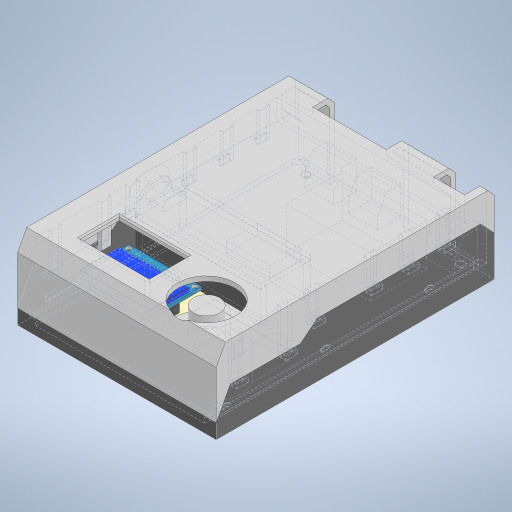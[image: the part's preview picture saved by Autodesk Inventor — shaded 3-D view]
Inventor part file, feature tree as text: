
AUTODESK INVENTOR PART (.ipt)
format: ipt  version: 2024.1 (Build 281209000, 209)  size: 1,683,456 bytes
history: native  units: mm
features: sketch x53, extrude x52, projected_geometry x36, chamfer x13, fillet x5, other x3, mirror x2, pattern_linear x1, plane x1
ambient origin geometry x8: Origin, YZ Plane, XZ Plane, XY Plane, X Axis, Y Axis, Z Axis, Center Point
bodies: Body1 (feature_tree), Body2 (feature_tree), Body3 (feature_tree)
feature tree (166):
  other  "pcb"
  extrude  "Extrusion1"  Depth=95.0mm
  chamfer  "Chamfer1"  Distance=1.57mm
  extrude  "Extrusion2"  Depth=10.8mm
  chamfer  "Chamfer2"  Distance=10.12mm
  chamfer  "Chamfer19"  Distance=3.0mm Angle=45.0deg
  chamfer  "Chamfer20"  Distance=15.0mm
  extrude  "Extrusion3"  Depth=1.2mm
  extrude  "Extrusion5"  Depth=17.9mm
  extrude  "Extrusion6"  Depth=2.44mm
  extrude  "Extrusion7"  Depth=0.1mm TaperAngle=0.0deg
  fillet  "Fillet1"  Radius=0.1mm
  fillet  "Fillet2"  Radius=5.0mm
  extrude  "Extrusion14"  Depth=5.0mm
  extrude  "Extrusion8"  Depth=3.2mm TaperAngle=0.0deg
  extrude  "Extrusion9"  Depth=2.0mm
  extrude  "Extrusion10"  Depth=2.37mm
  sketch  "Sketch12"  dims[d21=30.0mm d22=15.0mm d23=0.0mm]
  extrude  "Extrusion11"  Depth=10.2mm
  extrude  "Extrusion12"  Depth=0.1mm
  fillet  "Fillet3"  Radius=0.1mm
  extrude  "Extrusion13"  Depth=26.0mm
  extrude  "Extrusion88"  Depth=0.56mm
  extrude  "Extrusion89"  Depth=4.0mm
  fillet  "Fillet10"  Radius=16.58mm
  extrude  "Extrusion90"  Depth=0.1mm
  extrude  "Extrusion23"  Depth=0.1mm
  chamfer  "Chamfer3"  Distance=0.2mm
  pattern_linear  "Rectangular Pattern1"  Count1=2 Spacing1=55.0mm
  extrude  "CASE - START"  Depth=2.0mm
  extrude  "Extrusion25"  Depth=2.0mm
  extrude  "Extrusion26"  Depth=0.2mm
  chamfer  "Chamfer4"  Distance=1.64mm
  extrude  "Extrusion27"  Depth=0.5mm
  extrude  "Extrusion28"  Depth=13.0mm
  extrude  "Extrusion29"  Depth=0.5mm
  chamfer  "Chamfer5"  Distance=1.64mm
  fillet  "Fillet7"  Radius=4.0mm
  extrude  "Extrusion30"  Depth=1.5mm
  chamfer  "Chamfer6"  Distance=3.3mm
  extrude  "Extrusion33"  Depth=0.5mm TaperAngle=0.0deg
  extrude  "Extrusion35"  Depth=0.5mm
  chamfer  "Chamfer7"  Distance=0.5mm
  extrude  "Extrusion39"  Depth=0.5mm TaperAngle=0.0deg
  extrude  "Extrusion75"  Depth=0.5mm
  chamfer  "Chamfer9"  Distance=5.0mm
  extrude  "Extrusion79"  Depth=0.5mm
  extrude  "Extrusion80"  Depth=0.8mm
  extrude  "Extrusion81"  Depth=2.0mm TaperAngle=0.0deg
  extrude  "Extrusion91"  Depth=2.0mm TaperAngle=45.0deg
  extrude  "Extrusion83"  Depth=0.5mm
  extrude  "Extrusion53"  TaperAngle=0.0deg  [1 undecoded]
  extrude  "Extrusion92"  Depth=0.5mm
  extrude  "base-slots"  Depth=10.0mm
  extrude  "Extrusion62"  Depth=0.5mm
  extrude  "Extrusion63"  [1 undecoded]
  extrude  "Extrusion64"  Depth=0.5mm
  extrude  "Extrusion65"  Depth=0.5mm
  extrude  "Extrusion66"  Depth=0.5mm
  sketch  "Sketch78"  dims[d81=23.5mm]
  extrude  "Extrusion93"  Depth=0.5mm
  extrude  "Extrusion94"  Depth=2.0mm TaperAngle=0.0deg
  extrude  "Extrusion68"  Depth=2.0mm TaperAngle=45.0deg
  extrude  "Extrusion69"  Depth=1.5mm TaperAngle=0.0deg
  extrude  "Extrusion70"  Depth=0.5mm TaperAngle=0.0deg
  extrude  "Extrusion71"  Depth=2.0mm TaperAngle=45.0deg
  extrude  "Extrusion95"  Depth=0.5mm TaperAngle=0.0deg
  extrude  "Extrusion96"  Depth=0.5mm TaperAngle=45.0deg
  plane  "Work Plane1"
  chamfer  "Chamfer13"  Distance=10.0mm
  mirror  "Mirror1"
  mirror  "Mirror2"
  extrude  "Extrusion85"  Depth=1.5mm
  extrude  "Extrusion86"  Depth=2.0mm
  chamfer  "Chamfer15"  Distance=4.0mm
  chamfer  "Chamfer16"  Distance=4.0mm
  extrude  "Extrusion87"  Depth=2.0mm
  sketch  "Sketch1"  dims[d0=64.4mm d1=95.0mm]
  sketch  "Sketch2"  dims[d2=47.5mm]
  sketch  "Sketch3"  dims[d3=32.2mm d4=1.57mm d5=0.0mm]
  sketch  "Sketch5"  dims[d6=2.0mm d7=2.0mm d8=45.0deg d9=10.8mm]
  sketch  "Sketch7"  dims[d10=8.8mm]
  sketch  "Sketch8"  dims[d12=8.2mm d13=10.12mm d14=0.0mm d15=3.0mm d16=6.0mm d17=45.0deg]
  sketch  "Sketch9"  dims[d18=12.0mm]
  sketch  "Sketch10"  dims[d19=20.0mm]
  sketch  "Sketch11"  dims[d20=6.26mm]
  sketch  "Sketch13"  dims[d30=41.24mm d31=1.2mm]
  sketch  "Sketch14"  dims[d32=44.25mm d33=17.9mm]
  sketch  "Sketch15"  dims[d34=2.44mm d36=2.44mm]
  sketch  "Sketch17"  dims[d37=11.2mm d38=0.0mm d39=1.63mm d40=0.0mm d41=0.1mm d42=5.0mm]
  sketch  "Sketch26"  dims[d43=1.3mm d44=5.0mm]
  sketch  "Sketch28"  dims[d45=5.0mm d46=3.2mm d47=0.0mm]
  other  "case-bottom"
  sketch  "Sketch29"  dims[d48=2.0mm d49=3.0mm]
  projected_geometry  "Projected Loop2"
  sketch  "Sketch30"  dims[d50=10.29mm d51=2.37mm]
  sketch  "Sketch32"  dims[d52=17.0mm d53=10.2mm]
  sketch  "Sketch33"  dims[d54=10.9mm d55=0.0mm d56=9.0mm d57=0.1mm]
  sketch  "Sketch34"  dims[d58=26.0mm d59=25.94mm]
  projected_geometry  "Projected Loop3"
  sketch  "Sketch35"  dims[d60=1.06mm d61=0.0mm d62=0.56mm]
  projected_geometry  "Projected Loop4"
  projected_geometry  "Projected Loop5"
  sketch  "Sketch38"  dims[d63=0.56mm d64=4.0mm d65=16.58mm]
  sketch  "Sketch39"  dims[d66=1.3mm d67=0.0mm d68=0.1mm]
  projected_geometry  "Projected Loop9"
  projected_geometry  "Projected Loop11"
  other  "lid-1"
  sketch  "Sketch46"  dims[d69=0.1mm d70=0.1mm]
  projected_geometry  "Projected Loop14"
  projected_geometry  "Projected Loop15"
  projected_geometry  "Projected Loop16"
  projected_geometry  "Projected Loop17"
  projected_geometry  "Projected Loop18"
  projected_geometry  "Projected Loop19"
  sketch  "Sketch61"  dims[d71=14.0mm d72=0.2mm d73=0.0mm]
  sketch  "Sketch70"  dims[d74=7.0mm]
  sketch  "Sketch71"  dims[d75=7.0mm]
  sketch  "Sketch72"  dims[d76=0.2mm]
  sketch  "Sketch73"  dims[d77=0.2mm]
  sketch  "Sketch74"  dims[d78=0.2mm d79=0.0mm]
  sketch  "Sketch75"  dims[d80=2.0mm]
  projected_geometry  "Projected Loop52"
  sketch  "Sketch79"  dims[d82=23.5mm]
  projected_geometry  "Projected Loop54"
  sketch  "Sketch80"  dims[d83=1.9mm]
  sketch  "Sketch81"  dims[d84=1.22mm]
  sketch  "Sketch85"  dims[d85=1.22mm]
  sketch  "Sketch89"  dims[d86=1.25mm]
  sketch  "Sketch90"  dims[d87=1.25mm]
  projected_geometry  "Projected Loop68"
  projected_geometry  "Projected Loop69"
  sketch  "Sketch91"  dims[d88=0.0mm d89=0.0mm]
  sketch  "Sketch93"  dims[d90=3.6mm]
  projected_geometry  "Projected Loop75"
  sketch  "Sketch95"  dims[d91=3.6mm]
  projected_geometry  "Projected Loop76"
  sketch  "Sketch96"  dims[d92=15.5mm]
  projected_geometry  "Projected Loop77"
  projected_geometry  "Projected Loop78"
  projected_geometry  "Projected Loop79"
  projected_geometry  "Projected Loop80"
  sketch  "Sketch97"  dims[d93=0.1mm]
  projected_geometry  "Projected Loop81"
  sketch  "Sketch98"  dims[d94=3.8mm d95=0.0mm]
  sketch  "Sketch100"  dims[d139=5.31mm]
  sketch  "Sketch101"  dims[d140=5.31mm]
  projected_geometry  "Projected Loop82"
  projected_geometry  "Projected Loop83"
  projected_geometry  "Projected Loop84"
  projected_geometry  "Projected Loop85"
  sketch  "Sketch102"  dims[d141=1.37mm d142=0.0mm]
  projected_geometry  "Projected Loop86"
  projected_geometry  "Projected Loop87"
  projected_geometry  "Projected Loop88"
  projected_geometry  "Projected Loop89"
  sketch  "Sketch103"  dims[d143=1.0mm d144=4.0mm d145=45.0deg d146=20.0mm d148=55.0mm d149=20.0mm d151=87.0mm]
  projected_geometry  "Projected Loop90"
  sketch  "Sketch104"  dims[d152=2.0mm d153=2.0mm]
  projected_geometry  "Projected Loop91"
  sketch  "Sketch105"  dims[d154=2.0mm d155=3.0mm]
  projected_geometry  "Projected Loop92"
  sketch  "Sketch106"  dims[d156=2.0mm d157=0.0mm d158=0.2mm d159=1.64mm d160=0.0mm]
  projected_geometry  "Projected Loop93"
  sketch  "Sketch107"  dims[d161=5.0mm d162=20.0mm d163=13.0mm d164=8.0mm d165=1.64mm d166=0.0mm d167=1.0mm d168=4.0mm d169=45.0deg d171=1.5mm d172=3.3mm d173=1.64mm d174=0.0mm d175=2.2mm d176=0.5mm d177=1.64mm d178=0.0mm d180=5.0mm d181=5.0mm d182=5.0mm d183=0.8mm d184=2.0mm d185=0.0mm d186=2.0mm d187=4.0mm d188=45.0deg d189=0.5mm d191=0.0mm d192=9.0mm d194=10.0mm d195=9.445mm d196=-2.445mm d197=5.0mm d198=30.0mm d199=1.2mm d200=1.7mm d201=2.0mm d202=0.0mm d203=2.0mm d204=4.0mm d205=45.0deg d213=1.5mm d214=0.0mm d221=3.0mm d222=0.0mm d223=2.0mm d224=4.0mm d225=45.0deg d245=40.0mm d246=0.0mm d249=0.5mm d250=2.0mm d251=45.0deg d297=10.0mm d298=0.0mm d327=1.5mm d328=2.0mm d330=4.0mm d332=4.0mm d333=2.0mm d334=4.0mm d335=4.0mm d336=4.0mm d339=2.0mm d340=1.5mm d341=2.0mm d342=0.0mm d343=0.2mm d344=0.2mm d345=0.0mm d346=0.0mm d347=0.2mm d348=0.2mm d349=0.0mm d350=0.2mm d351=0.2mm d352=0.2mm d353=0.2mm d354=1.1mm d355=0.0mm d356=1.0mm d357=1.0mm d358=1.1mm d359=0.0mm d360=10.0mm d361=0.0mm d362=1.0mm d363=1.0mm d364=10.0mm d365=0.0mm d366=10.0mm d367=0.0mm d372=0.6mm d373=2.0mm d374=45.0deg d376=1.47mm d377=0.2mm d378=0.64mm d379=1.5mm d380=0.0mm d381=10.0mm d382=0.0mm d383=0.2mm d384=1.47mm d385=0.64mm d386=10.0mm d387=0.0mm d388=10.0mm d389=0.0mm d390=0.59mm d405=9.0mm d406=8.0mm d410=8.0mm d411=1.7mm d413=40.0mm d414=0.0mm d425=10.0mm d426=0.0mm d428=1.7mm d429=3.0mm d430=0.0mm d431=10.0mm d432=0.0mm d436=10.0mm d437=0.0mm d438=0.39mm d439=3.11mm d452=0.1mm d453=1.7mm d454=1.7mm d455=4.0mm d456=0.0mm d457=4.0mm d458=1.0mm d459=0.0mm d460=0.55mm d461=2.0mm d462=45.0deg d463=0.55mm d464=2.0mm d465=45.0deg d466=0.5mm d467=0.0mm d474=10.52mm d475=10.52mm d476=10.52mm d477=0.01mm d478=5.17mm d479=3.0mm d480=6.0mm d481=45.0deg d482=3.0mm d483=6.0mm d484=45.0deg d485=9.4mm d486=13.2mm d487=11.07mm d488=21.5mm d489=0.0mm d490=23.7mm d491=20.42mm d492=12.82mm d493=11.7mm d494=0.0mm d495=8.0mm d496=3.2mm d497=0.7mm d498=11.0mm d499=4.4mm d500=0.0mm d501=25.0mm d502=8.201332mm d503=8.201332mm d504=1.0mm d505=0.5mm d506=1.7mm d507=1.7mm d508=1.7mm d509=1.7mm d510=10.0mm d511=0.0mm d514=20.5mm d515=8.726646mm d516=1.7mm d517=10.0mm d518=0.0mm d519=4.0mm d520=4.0mm d521=9.0mm d522=9.0mm d523=0.2mm d524=0.2mm d525=0.2mm d526=0.2mm d527=1.1mm d528=0.0mm d529=10.0mm d530=0.0mm d531=10.0mm d532=0.0mm d533=10.0mm d534=0.0mm d247=0.5mm d248=0.872665mm d296=0.5mm d299=0.872665mm d433=0.5mm d434=0.872665mm]
  projected_geometry  "Projected Loop94"
note: 2 required parameter values undecoded (feature->parameter linkage not recoverable at this tier; creation-order binding heuristic only, values carry confidence <= 0.55)
